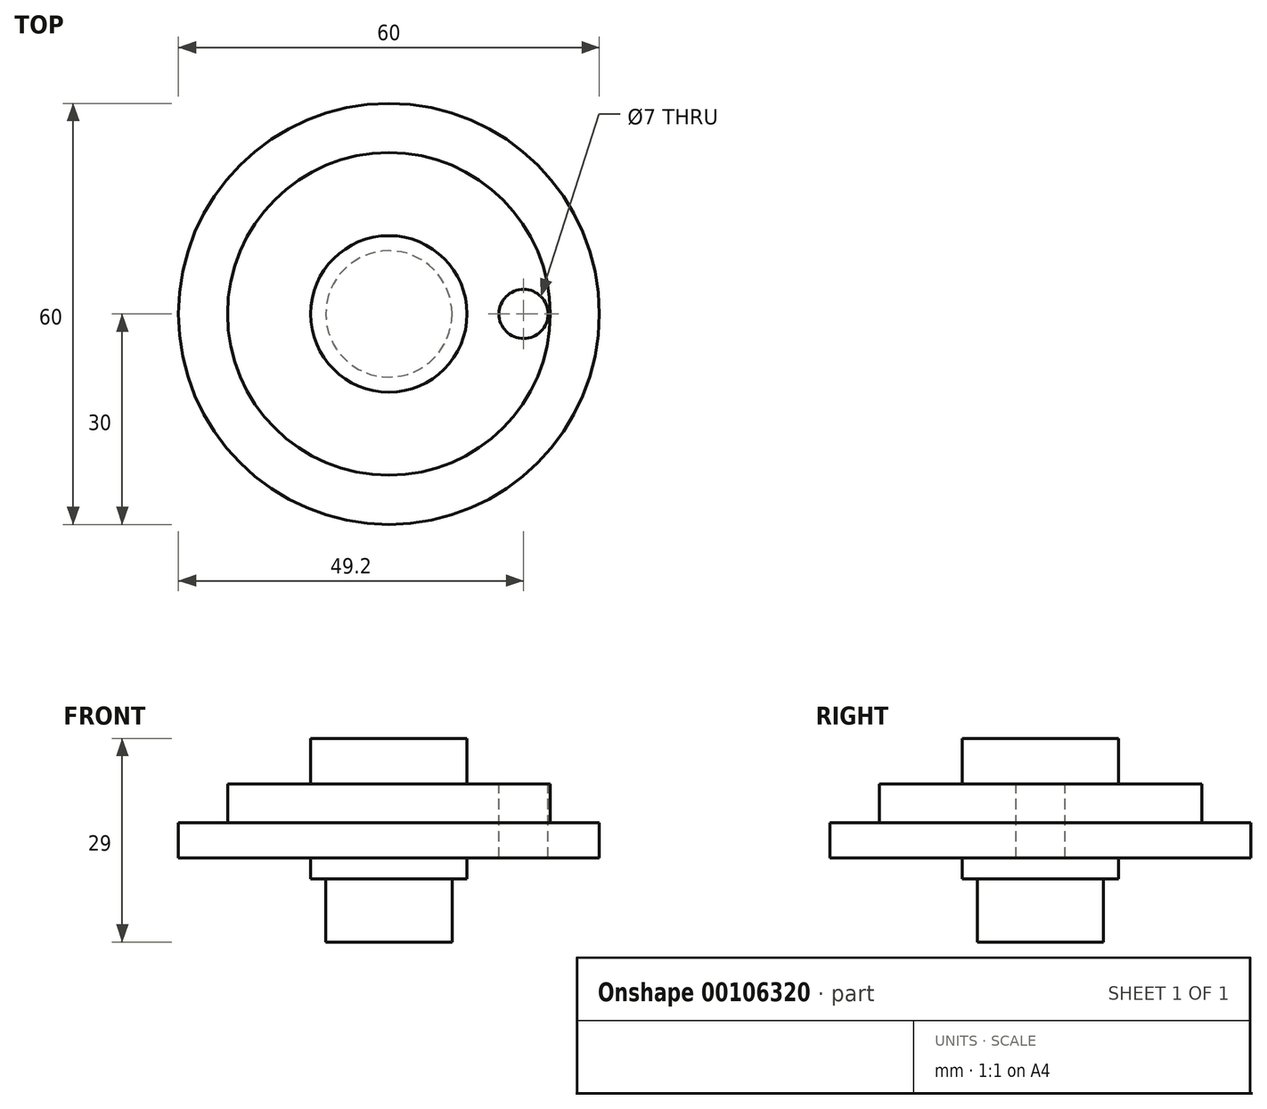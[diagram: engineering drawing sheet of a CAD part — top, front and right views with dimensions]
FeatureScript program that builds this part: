
annotation { "Feature Type Name" : "Feature", "Feature Type Description" : "" }
export const myFeature = defineFeature(function(context is Context, id is Id, definition is map)
    precondition{}
    {
        {
            var Q0;
            Q0=qCreatedBy(makeId("Top.planeOp"),FACE);
            var sketch = newSketch(context, id + "F0", { "sketchPlane" : qUnion([Q0])});
            skCircle(sketch, "E0", {"center": v(0, 0) * mm, "radius": 30 * mm});
            skSolve(sketch);
        }
        {
            var Q0;
            Q0=makeQuery(id+"F0.imprint","IMPRINT",FACE,{"disambiguationData":[TD([[makeQuery(id+"F0.imprint","IMPRINT",EDGE,{"derivedFrom":sQuery(id+"F0.wireOp",EDGE,"E0")}),1.0]])]});
            extrude(context, id + "F1", {"entities" : qUnion([Q0]), "depth" : 5 * mm});
        }
        {
            var Q0;
            Q0=makeQuery(id+"F1.opExtrude","CAP_FACE",FACE,{"disambiguationData":[OSD([sQuery(id+"F0.wireOp",EDGE,"E0")])],"isStart":false});
            var sketch = newSketch(context, id + "F2", { "sketchPlane" : qUnion([Q0])});
            skCircle(sketch, "E1", {"center": v(0, 0) * mm, "radius": 11.15 * mm});
            skSolve(sketch);
        }
        {
            var Q0;
            Q0=makeQuery(id+"F2.imprint","IMPRINT",FACE,{"disambiguationData":[TD([[makeQuery(id+"F2.imprint","IMPRINT",EDGE,{"derivedFrom":sQuery(id+"F2.wireOp",EDGE,"E1")}),1.0]])]});
            extrude(context, id + "F3", {"entities" : qUnion([Q0]), "operationType" : NewBodyOperationType.ADD, "depth" : 12 * mm, "hasSecondDirection" : true, "secondDirectionOppositeDirection" : true, "secondDirectionDepth" : 8 * mm});
        }
        {
            var Q0;
            Q0=makeQuery(id+"F3.opExtrude","CAP_FACE",FACE,{"disambiguationData":[OSD([sQuery(id+"F2.wireOp",EDGE,"E1")])],"isStart":true});
            var sketch = newSketch(context, id + "F4", { "sketchPlane" : qUnion([Q0])});
            skCircle(sketch, "E2", {"center": v(0, 0) * mm, "radius": 9 * mm});
            skSolve(sketch);
        }
        {
            var Q0;
            Q0=makeQuery(id+"F4.imprint","IMPRINT",FACE,{"disambiguationData":[TD([[makeQuery(id+"F4.imprint","IMPRINT",EDGE,{"derivedFrom":sQuery(id+"F4.wireOp",EDGE,"E2")}),1.0]])]});
            extrude(context, id + "F5", {"entities" : qUnion([Q0]), "operationType" : NewBodyOperationType.ADD, "depth" : 9 * mm});
        }
        {
            var Q0;
            Q0=makeQuery(id+"F1.opExtrude","CAP_FACE",FACE,{"disambiguationData":[OSD([sQuery(id+"F0.wireOp",EDGE,"E0")])],"isStart":false});
            var sketch = newSketch(context, id + "F6", { "sketchPlane" : qUnion([Q0])});
            skCircle(sketch, "E3", {"center": v(0, 0) * mm, "radius": 23 * mm});
            skSolve(sketch);
        }
        {
            var Q0;
            Q0=makeQuery(id+"F6.imprint","IMPRINT",FACE,{"disambiguationData":[TD([[makeQuery(id+"F6.imprint","IMPRINT",EDGE,{"derivedFrom":sQuery(id+"F6.wireOp",EDGE,"E3")}),1.0]])]});
            extrude(context, id + "F7", {"entities" : qUnion([Q0]), "operationType" : NewBodyOperationType.ADD, "depth" : 5.5 * mm});
        }
        {
            var Q0;
            Q0=makeQuery(id+"F1.opExtrude","CAP_FACE",FACE,{"disambiguationData":[OSD([sQuery(id+"F0.wireOp",EDGE,"E0")])],"isStart":false});
            var sketch = newSketch(context, id + "F8", { "sketchPlane" : qUnion([Q0])});
            skLineSegment(sketch, "E4", {"start": v(0, 0) * mm, "end": v(19.2, 0) * mm, "construction": true});
            skCircle(sketch, "E5", {"center": v(19.2, 0) * mm, "radius": 3.5 * mm});
            skSolve(sketch);
        }
        {
            var Q0;
            Q0 = qSketchRegion(id + "F8", true);
            extrude(context, id + "F9", {"entities" : qUnion([Q0]), "operationType" : NewBodyOperationType.REMOVE, "endBound" : BoundingType.SYMMETRIC, "oppositeDirection" : true, "depth" : 25 * mm});
        }
    });
